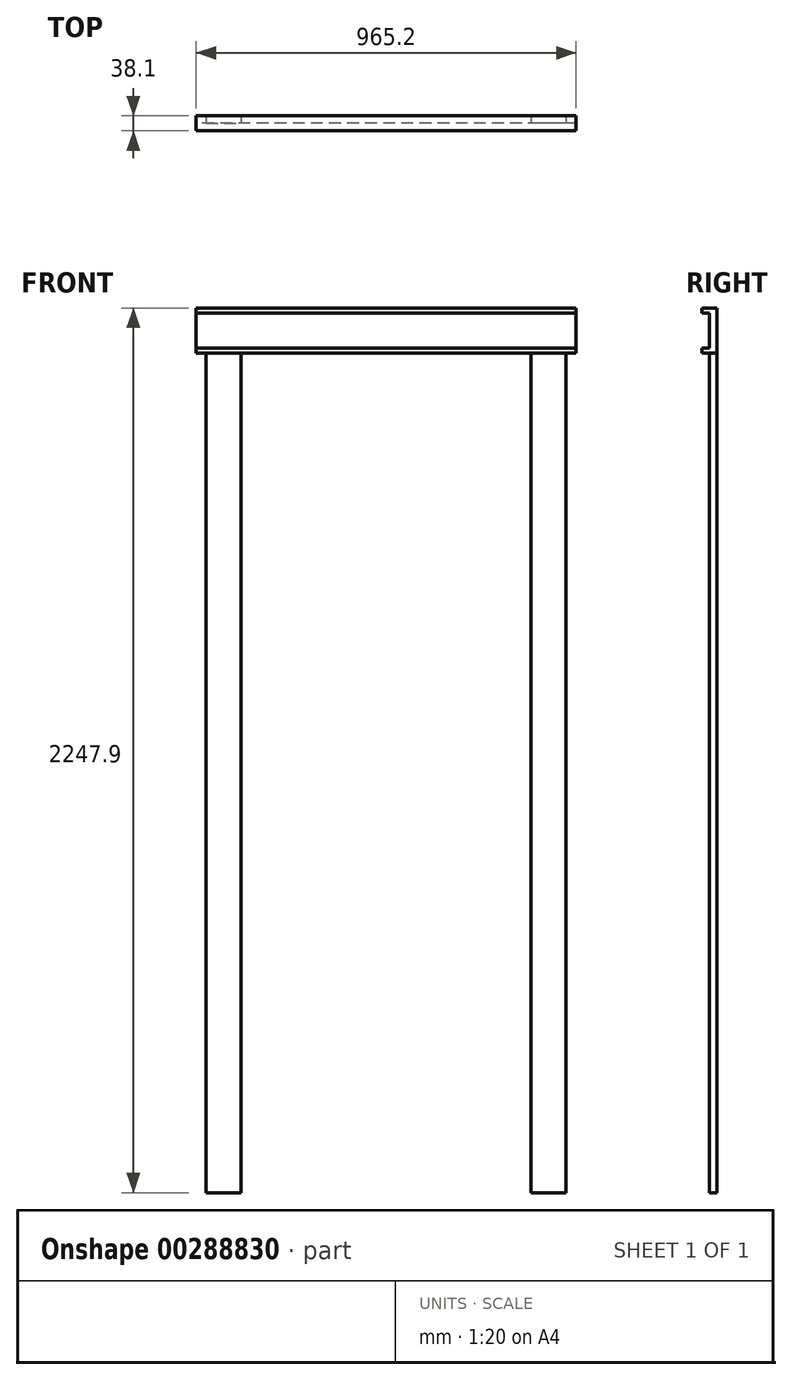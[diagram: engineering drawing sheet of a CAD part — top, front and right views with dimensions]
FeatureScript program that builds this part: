
annotation { "Feature Type Name" : "Feature", "Feature Type Description" : "" }
export const myFeature = defineFeature(function(context is Context, id is Id, definition is map)
    precondition{}
    {
        {
            var Q0;
            Q0=qCreatedBy(makeId("Right.planeOp"),FACE);
            var sketch = newSketch(context, id + "F0", { "sketchPlane" : qUnion([Q0])});
            skLineSegment(sketch, "E0.bottom", {"start": v(0, 0) * mm, "end": v(38.1, 0) * mm});
            skLineSegment(sketch, "E0.top", {"start": v(0, 12.7) * mm, "end": v(38.1, 12.7) * mm});
            skLineSegment(sketch, "E0.left", {"start": v(0, 0) * mm, "end": v(0, 12.7) * mm});
            skLineSegment(sketch, "E0.right", {"start": v(38.1, 0) * mm, "end": v(38.1, 12.7) * mm});
            skLineSegment(sketch, "E1.bottom", {"start": v(19.05, 12.7) * mm, "end": v(38.1, 12.7) * mm});
            skLineSegment(sketch, "E1.top", {"start": v(19.05, 101.6) * mm, "end": v(38.1, 101.6) * mm});
            skLineSegment(sketch, "E1.left", {"start": v(19.05, 12.7) * mm, "end": v(19.05, 101.6) * mm});
            skLineSegment(sketch, "E1.right", {"start": v(38.1, 12.7) * mm, "end": v(38.1, 101.6) * mm});
            skLineSegment(sketch, "E2.bottom", {"start": v(38.1, 101.6) * mm, "end": v(0, 101.6) * mm});
            skLineSegment(sketch, "E2.top", {"start": v(38.1, 114.3) * mm, "end": v(0, 114.3) * mm});
            skLineSegment(sketch, "E2.left", {"start": v(38.1, 101.6) * mm, "end": v(38.1, 114.3) * mm});
            skLineSegment(sketch, "E2.right", {"start": v(0, 101.6) * mm, "end": v(0, 114.3) * mm});
            skSolve(sketch);
        }
        {
            var Q0;
            Q0 = qSketchRegion(id + "F0", true);
            extrude(context, id + "F1", {"entities" : qUnion([Q0]), "depth" : 965.2 * mm});
        }
        {
            var Q0;
            Q0=makeQuery(id+"F1.opExtrude","SWEPT_FACE",FACE,{"disambiguationData":[OSD([sQuery(id+"F0.wireOp",EDGE,"E0.bottom")])]});
            var sketch = newSketch(context, id + "F2", { "sketchPlane" : qUnion([Q0])});
            skLineSegment(sketch, "E3.bottom", {"start": v(25.4, -38.1) * mm, "end": v(114.3, -38.1) * mm});
            skLineSegment(sketch, "E3.top", {"start": v(25.4, -19.05) * mm, "end": v(114.3, -19.05) * mm});
            skLineSegment(sketch, "E3.left", {"start": v(25.4, -38.1) * mm, "end": v(25.4, -19.05) * mm});
            skLineSegment(sketch, "E3.right", {"start": v(114.3, -38.1) * mm, "end": v(114.3, -19.05) * mm});
            skLineSegment(sketch, "E4.bottom", {"start": v(939.8, -38.1) * mm, "end": v(850.9, -38.1) * mm});
            skLineSegment(sketch, "E4.top", {"start": v(939.8, -19.05) * mm, "end": v(850.9, -19.05) * mm});
            skLineSegment(sketch, "E4.left", {"start": v(939.8, -38.1) * mm, "end": v(939.8, -19.05) * mm});
            skLineSegment(sketch, "E4.right", {"start": v(850.9, -38.1) * mm, "end": v(850.9, -19.05) * mm});
            skSolve(sketch);
        }
        {
            var Q0;
            Q0 = qSketchRegion(id + "F2", true);
            extrude(context, id + "F3", {"entities" : qUnion([Q0]), "operationType" : NewBodyOperationType.ADD, "depth" : 2133.6 * mm});
        }
    });
